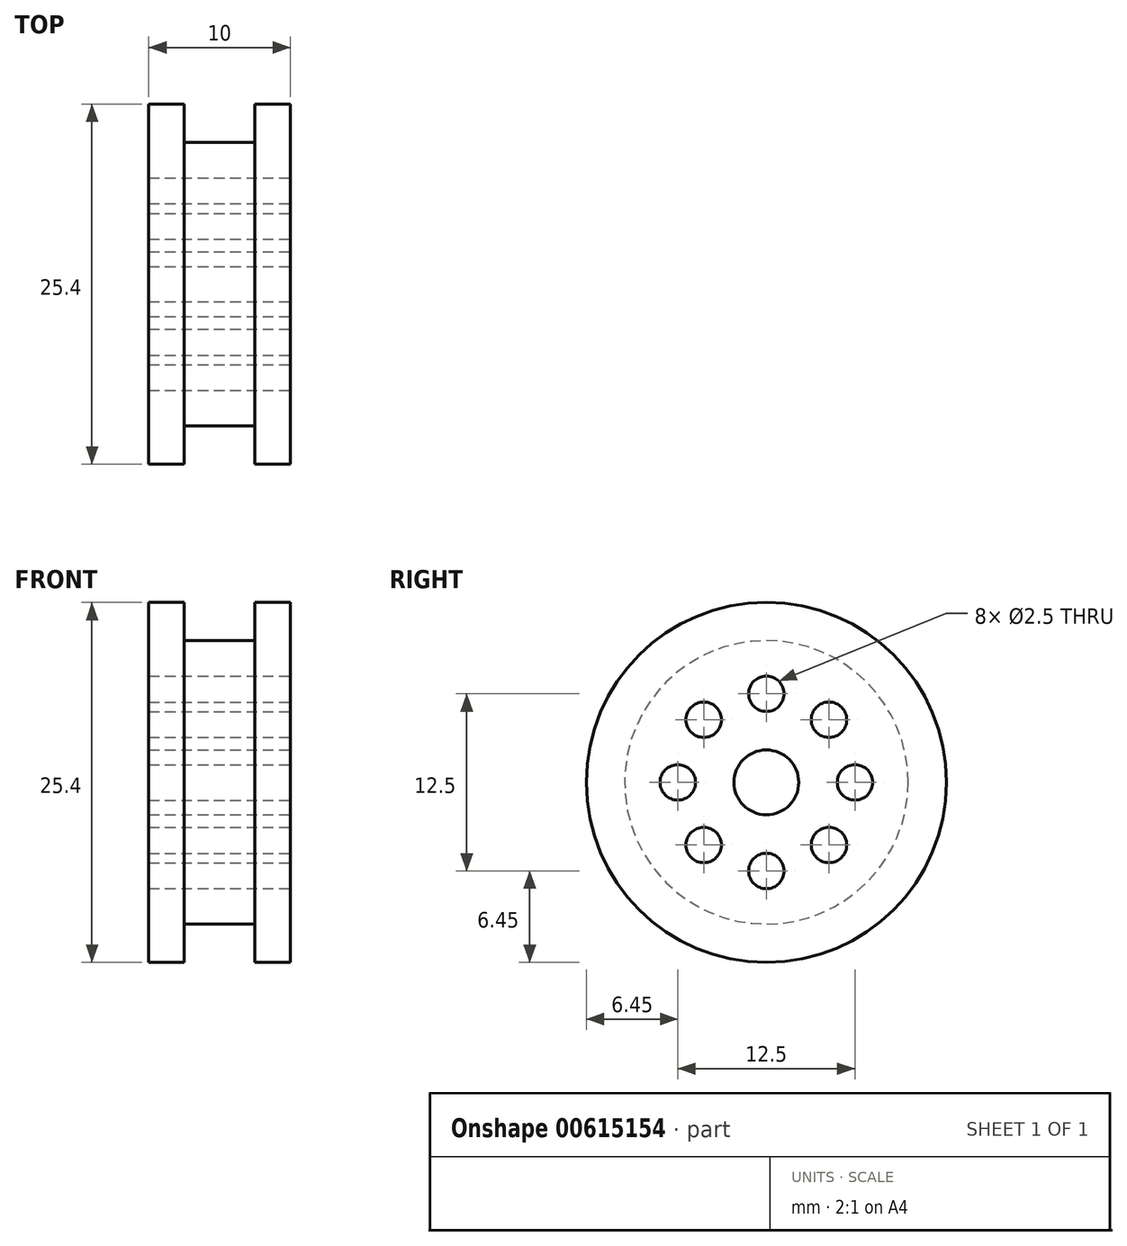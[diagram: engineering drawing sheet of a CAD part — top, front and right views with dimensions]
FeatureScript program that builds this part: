
annotation { "Feature Type Name" : "Feature", "Feature Type Description" : "" }
export const myFeature = defineFeature(function(context is Context, id is Id, definition is map)
    precondition{}
    {
        {
            var Q0;
            Q0=qCreatedBy(makeId("Right.planeOp"),FACE);
            var sketch = newSketch(context, id + "F0", { "sketchPlane" : qUnion([Q0])});
            skCircle(sketch, "E0", {"center": v(0, 0) * mm, "radius": 10 * mm});
            skSolve(sketch);
        }
        {
            var Q0;
            Q0=makeQuery(id+"F0.imprint","IMPRINT",FACE,{"disambiguationData":[TD([[makeQuery(id+"F0.imprint","IMPRINT",EDGE,{"derivedFrom":sQuery(id+"F0.wireOp",EDGE,"E0")}),1.0]])]});
            extrude(context, id + "F1", {"entities" : qUnion([Q0]), "depth" : 2.5 * mm, "offsetDistance" : 25 * mm});
        }
        {
            var Q0;
            Q0=makeQuery(id+"F1.opExtrude","CAP_FACE",FACE,{"disambiguationData":[OSD([sQuery(id+"F0.wireOp",EDGE,"E0")])],"isStart":false});
            var sketch = newSketch(context, id + "F2", { "sketchPlane" : qUnion([Q0])});
            skCircle(sketch, "E1", {"center": v(0, 0) * mm, "radius": 12.7 * mm});
            skSolve(sketch);
        }
        {
            var Q0;
            Q0 = qSketchRegion(id + "F2", true);
            extrude(context, id + "F3", {"entities" : qUnion([Q0]), "operationType" : NewBodyOperationType.ADD, "depth" : 2.5 * mm, "offsetDistance" : 25 * mm});
        }
        {
            var Q0;
            Q0=makeQuery(id+"F1.opExtrude","SWEPT_BODY",BODY,{"disambiguationData":[OSD([sQuery(id+"F0.wireOp",EDGE,"E0")])]});
            var Q1;
            Q1=makeQuery(id+"F1.opExtrude","CAP_FACE",FACE,{"disambiguationData":[OSD([sQuery(id+"F0.wireOp",EDGE,"E0")])],"isStart":true});
            mirror(context, id + "F4", {"operationType" : NewBodyOperationType.ADD, "entities" : qUnion([Q0]), "mirrorPlane" : qUnion([Q1])});
        }
        {
            var Q0;
            Q0=makeQuery(id+"F3.opExtrude","CAP_FACE",FACE,{"disambiguationData":[OSD([sQuery(id+"F2.wireOp",EDGE,"E1")])],"isStart":false});
            var sketch = newSketch(context, id + "F5", { "sketchPlane" : qUnion([Q0])});
            skCircle(sketch, "E2", {"center": v(0, 0) * mm, "radius": 2.29 * mm});
            skSolve(sketch);
        }
        {
            var Q0;
            Q0=makeQuery(id+"F5.imprint","IMPRINT",FACE,{"disambiguationData":[TD([[makeQuery(id+"F5.imprint","IMPRINT",EDGE,{"derivedFrom":sQuery(id+"F5.wireOp",EDGE,"E2")}),1.0]])]});
            extrude(context, id + "F6", {"entities" : qUnion([Q0]), "operationType" : NewBodyOperationType.REMOVE, "endBound" : BoundingType.THROUGH_ALL, "oppositeDirection" : true, "depth" : 25 * mm, "offsetDistance" : 25 * mm});
        }
        {
            var Q0;
            Q0=makeQuery(id+"F3.opExtrude","CAP_FACE",FACE,{"disambiguationData":[OSD([sQuery(id+"F2.wireOp",EDGE,"E1")])],"isStart":false});
            var sketch = newSketch(context, id + "F7", { "sketchPlane" : qUnion([Q0])});
            skCircle(sketch, "E3", {"center": v(0, 0) * mm, "radius": 6.25 * mm, "construction": true});
            skCircle(sketch, "E4", {"center": v(0, 6.25) * mm, "radius": 1.25 * mm});
            skCircle(sketch, "E5", {"center": v(6.25, 0) * mm, "radius": 1.25 * mm});
            skCircle(sketch, "E6", {"center": v(0, -6.25) * mm, "radius": 1.25 * mm});
            skCircle(sketch, "E7", {"center": v(-6.25, 0) * mm, "radius": 1.25 * mm});
            skLineSegment(sketch, "E8", {"start": v(6.25, 6.25) * mm, "end": v(6.25, -6.25) * mm, "construction": true});
            skLineSegment(sketch, "E9", {"start": v(6.25, -6.25) * mm, "end": v(-6.25, -6.25) * mm, "construction": true});
            skLineSegment(sketch, "E10", {"start": v(-6.25, -6.25) * mm, "end": v(-6.25, 6.25) * mm, "construction": true});
            skLineSegment(sketch, "E11", {"start": v(-6.25, 6.25) * mm, "end": v(6.25, 6.25) * mm, "construction": true});
            skLineSegment(sketch, "E12", {"start": v(6.25, 6.25) * mm, "end": v(-6.25, -6.25) * mm, "construction": true});
            skLineSegment(sketch, "E13", {"start": v(-6.25, 6.25) * mm, "end": v(6.25, -6.25) * mm, "construction": true});
            skCircle(sketch, "E14", {"center": v(-4.42, -4.42) * mm, "radius": 1.25 * mm});
            skCircle(sketch, "E15", {"center": v(4.42, -4.42) * mm, "radius": 1.25 * mm});
            skCircle(sketch, "E16", {"center": v(-4.42, 4.42) * mm, "radius": 1.25 * mm});
            skCircle(sketch, "E17", {"center": v(4.42, 4.42) * mm, "radius": 1.25 * mm});
            skSolve(sketch);
        }
        {
            var Q0;
            Q0 = qSketchRegion(id + "F7", true);
            extrude(context, id + "F8", {"entities" : qUnion([Q0]), "operationType" : NewBodyOperationType.REMOVE, "endBound" : BoundingType.THROUGH_ALL, "oppositeDirection" : true, "depth" : 25 * mm, "offsetDistance" : 25 * mm});
        }
    });
